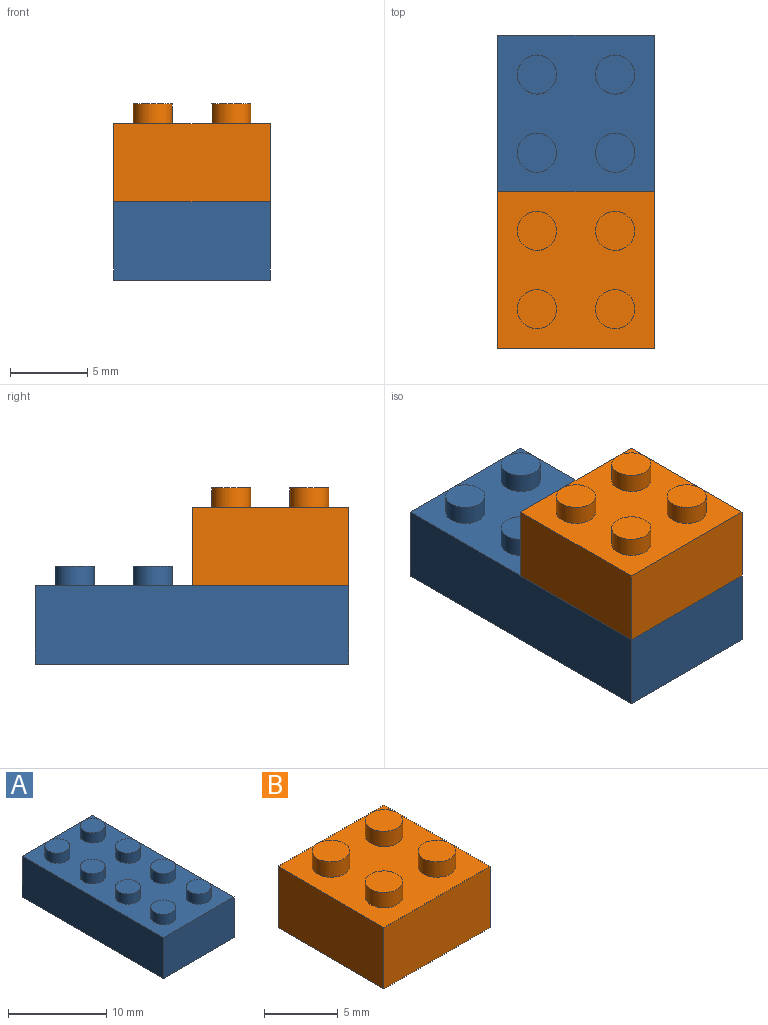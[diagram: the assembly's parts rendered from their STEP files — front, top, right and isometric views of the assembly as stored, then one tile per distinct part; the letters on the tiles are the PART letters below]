
ASSEMBLY  parts=2 mates=1
PART A: 27 faces, bbox 10.2x20.3x6.4 mm
  f0: plane 20.32x10.16mm, normal (0,0,-1), area 71mm2, adj f1,f2,f3,f4,f22,f23,f24,f25
  f1: plane 20.32x5.08mm, normal (-1,0,0), area 103.2mm2, adj f0,f2,f4,f5
  f2: plane 10.16x5.08mm, normal (0,-1,0), area 51.6mm2, adj f0,f1,f3,f5
  f3: plane 20.32x5.08mm, normal (1,0,0), area 103.2mm2, adj f0,f2,f4,f5
  f4: plane 10.16x5.08mm, normal (0,1,0), area 51.6mm2, adj f0,f1,f3,f5
  f5: plane 20.32x10.16mm, normal (0,0,1), area 165.9mm2, adj f1,f2,f3,f4,f6,f8,f10,f12
  f6: cylinder r=1.27mm len=2.54mm, axis (0,0,-1), area 10.1mm2, adj f5,f7
  f7: plane 2.54x2.54mm, normal (0,0,1), area 5.1mm2, adj f6
  f8: cylinder r=1.27mm len=2.54mm, axis (0,0,-1), area 10.1mm2, adj f5,f9
  f9: plane 2.54x2.54mm, normal (0,0,1), area 5.1mm2, adj f8
  f10: cylinder r=1.27mm len=2.54mm, axis (0,0,-1), area 10.1mm2, adj f5,f11
  f11: plane 2.54x2.54mm, normal (0,0,1), area 5.1mm2, adj f10
  f12: cylinder r=1.27mm len=2.54mm, axis (0,0,-1), area 10.1mm2, adj f5,f13
  f13: plane 2.54x2.54mm, normal (0,0,1), area 5.1mm2, adj f12
  f14: cylinder r=1.27mm len=2.54mm, axis (0,0,-1), area 10.1mm2, adj f5,f15
  f15: plane 2.54x2.54mm, normal (0,0,1), area 5.1mm2, adj f14
  f16: cylinder r=1.27mm len=2.54mm, axis (0,0,-1), area 10.1mm2, adj f5,f17
  f17: plane 2.54x2.54mm, normal (0,0,1), area 5.1mm2, adj f16
  f18: cylinder r=1.27mm len=2.54mm, axis (0,0,-1), area 10.1mm2, adj f5,f19
  f19: plane 2.54x2.54mm, normal (0,0,1), area 5.1mm2, adj f18
  f20: cylinder r=1.27mm len=2.54mm, axis (0,0,-1), area 10.1mm2, adj f5,f21
  f21: plane 2.54x2.54mm, normal (0,0,1), area 5.1mm2, adj f20
  f22: plane 17.78x3.81mm, normal (-1,0,0), area 67.7mm2, adj f0,f23,f25,f26
  f23: plane 7.62x3.81mm, normal (0,1,0), area 29mm2, adj f0,f22,f24,f26
  f24: plane 17.78x3.81mm, normal (1,0,0), area 67.7mm2, adj f0,f23,f25,f26
  f25: plane 7.62x3.81mm, normal (0,-1,0), area 29mm2, adj f0,f22,f24,f26
  f26: plane 17.78x7.62mm, normal (0,0,-1), area 135.5mm2, adj f22,f23,f24,f25
PART B: 14 faces, bbox 10.2x10.2x6.4 mm
  f0: plane 10.16x5.08mm, normal (-1,0,0), area 51.6mm2, adj f1,f3,f4,f13
  f1: plane 10.16x5.08mm, normal (0,-1,0), area 51.6mm2, adj f0,f2,f3,f4
  f2: plane 10.16x5.08mm, normal (1,0,0), area 51.6mm2, adj f1,f3,f4,f13
  f3: plane 10.16x10.16mm, normal (0,0,1), area 83mm2, adj f0,f1,f2,f5,f7,f9,f11,f13
  f4: plane 10.16x10.16mm, normal (0,0,-1), area 103.2mm2, adj f0,f1,f2,f13
  f5: cylinder r=1.27mm len=2.54mm, axis (0,0,-1), area 10.1mm2, adj f3,f6
  f6: plane 2.54x2.54mm, normal (0,0,1), area 5.1mm2, adj f5
  f7: cylinder r=1.27mm len=2.54mm, axis (0,0,-1), area 10.1mm2, adj f3,f8
  f8: plane 2.54x2.54mm, normal (0,0,1), area 5.1mm2, adj f7
  f9: cylinder r=1.27mm len=2.54mm, axis (0,0,-1), area 10.1mm2, adj f3,f10
  f10: plane 2.54x2.54mm, normal (0,0,1), area 5.1mm2, adj f9
  f11: cylinder r=1.27mm len=2.54mm, axis (0,0,-1), area 10.1mm2, adj f3,f12
  f12: plane 2.54x2.54mm, normal (0,0,1), area 5.1mm2, adj f11
  f13: plane 10.16x5.08mm, normal (0,1,0), area 51.6mm2, adj f0,f2,f3,f4
PLACE A t=(12.43,0.34,-3.81)mm
PLACE B t=(12.43,0.34,1.27)mm
MATE fastened A.f5 <-> B.f4  axis (0,0,1) through (12.43,0.34,1.27)mm
